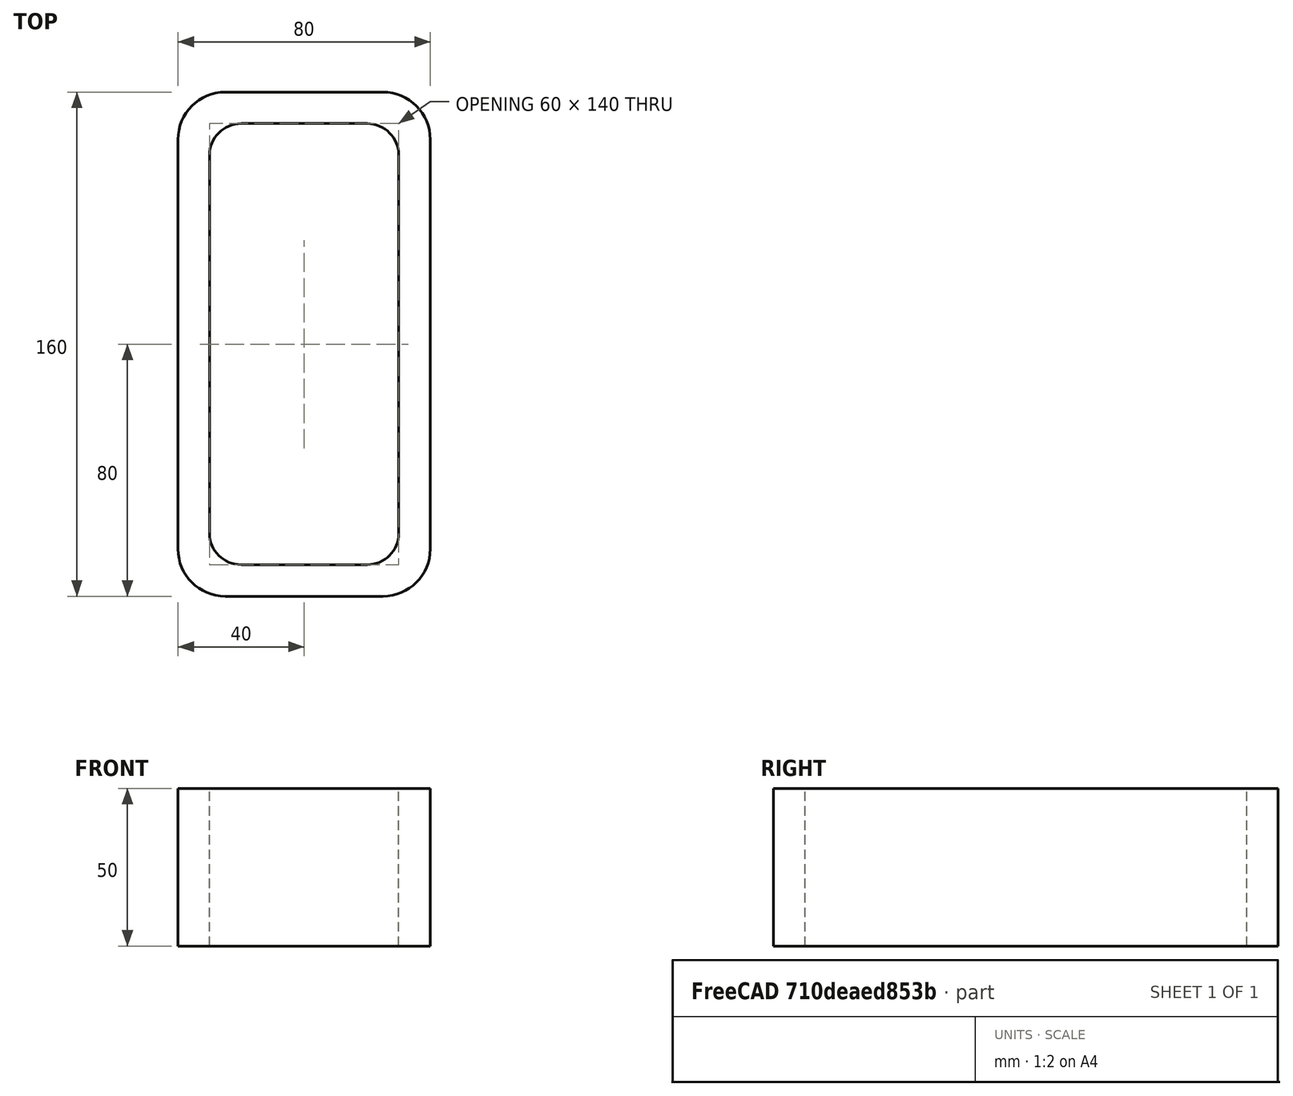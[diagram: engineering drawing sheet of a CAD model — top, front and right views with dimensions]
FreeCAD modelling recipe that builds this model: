
FCSTD DOCUMENT  (FreeCAD 0.15R4671 (Git))
Label: Rectangular hollow section 160x80x10 EN10219 S235JRH
License: All rights reserved
LicenseURL: http://en.wikipedia.org/wiki/All_rights_reserved
objects: Sketcher::SketchObject×1, Part::Extrusion×1
note: 2 computed .brp shape members not serialized (recipe doc carries the construction recipe); baked Part::Feature solids carry a one-line shape summary decoded from their .brp

FEATURE [Sketcher::SketchObject] Sketch
  sketch-geometry (16):
    g0: LineSegment StartX=-20 StartY=70 StartZ=0 EndX=20 EndY=70 EndZ=0
    g1: LineSegment StartX=30 StartY=60 StartZ=0 EndX=30 EndY=-60 EndZ=0
    g2: LineSegment StartX=20 StartY=-70 StartZ=0 EndX=-20 EndY=-70 EndZ=0
    g3: LineSegment StartX=-30 StartY=-60 StartZ=0 EndX=-30 EndY=60 EndZ=0
    g4: LineSegment StartX=-25 StartY=80 StartZ=0 EndX=25 EndY=80 EndZ=0
    g5: LineSegment StartX=40 StartY=65 StartZ=0 EndX=40 EndY=-65 EndZ=0
    g6: LineSegment StartX=25 StartY=-80 StartZ=0 EndX=-25 EndY=-80 EndZ=0
    g7: LineSegment StartX=-40 StartY=-65 StartZ=0 EndX=-40 EndY=65 EndZ=0
    g8: ArcOfCircle CenterX=-20 CenterY=60 CenterZ=0 NormalX=0 NormalY=0 NormalZ=1 Radius=10 StartAngle=1.5708 EndAngle=3.14159
    g9: ArcOfCircle CenterX=20 CenterY=60 CenterZ=0 NormalX=0 NormalY=0 NormalZ=1 Radius=10 StartAngle=0 EndAngle=1.5708
    g10: ArcOfCircle CenterX=20 CenterY=-60 CenterZ=0 NormalX=0 NormalY=0 NormalZ=1 Radius=10 StartAngle=4.71239 EndAngle=6.28319
    g11: ArcOfCircle CenterX=-20 CenterY=-60 CenterZ=0 NormalX=0 NormalY=0 NormalZ=1 Radius=10 StartAngle=3.14159 EndAngle=4.71239
    g12: ArcOfCircle CenterX=25 CenterY=65 CenterZ=0 NormalX=0 NormalY=0 NormalZ=1 Radius=15 StartAngle=0 EndAngle=1.5708
    g13: ArcOfCircle CenterX=25 CenterY=-65 CenterZ=0 NormalX=0 NormalY=0 NormalZ=1 Radius=15 StartAngle=4.71239 EndAngle=6.28319
    g14: ArcOfCircle CenterX=-25 CenterY=-65 CenterZ=0 NormalX=0 NormalY=0 NormalZ=1 Radius=15 StartAngle=3.14159 EndAngle=4.71239
    g15: ArcOfCircle CenterX=-25 CenterY=65 CenterZ=0 NormalX=0 NormalY=0 NormalZ=1 Radius=15 StartAngle=1.5708 EndAngle=3.14159
  constraints (36):
    c: Horizontal(g2)
    c: Vertical(g3)
    c: Horizontal(g6)
    c: Vertical(g7)
    c: Tangent(g3,g8) = 1.5708
    c: Tangent(g0,g8) = 1.5708
    c: Tangent(g0,g9) = 1.5708
    c: Tangent(g1,g9) = 1.5708
    c: Tangent(g1,g10) = 1.5708
    c: Tangent(g2,g10) = 1.5708
    c: Tangent(g2,g11) = 1.5708
    c: Tangent(g3,g11) = 1.5708
    c: Tangent(g4,g12) = 1.5708
    c: Tangent(g5,g12) = 1.5708
    c: Tangent(g5,g13) = 1.5708
    c: Tangent(g6,g13) = 1.5708
    c: Tangent(g6,g14) = 1.5708
    c: Tangent(g7,g14) = 1.5708
    c: Tangent(g7,g15) = 1.5708
    c: Tangent(g4,g15) = 1.5708
    c: Equal(g9,g8)
    c: Equal(g9,g11)
    c: Equal(g9,g10)
    c: Equal(g12,g15)
    c: Equal(g12,g14)
    c: Equal(g12,g13)
    c: Symmetric(g4,g6,g-1)
    c: Symmetric(g7,g5,g-2)
    c: DistanceY(g4,g6) = -160
    c: DistanceX(g7,g5) = 80
    c: Symmetric(g3,g1,g-2)
    c: Symmetric(g0,g2,g-1)
    c: DistanceY(g0,g4) = 10
    c: DistanceX(g5,g1) = -10
    c: Radius(g9) = 10
    c: Radius(g12) = 15
FEATURE [Part::Extrusion] Extrude  label="Rectangular hollow section 160x80x10 EN10219 S235JRH"
  Base = -> Sketch
  Dir = (0,0,50)
  Solid = true
